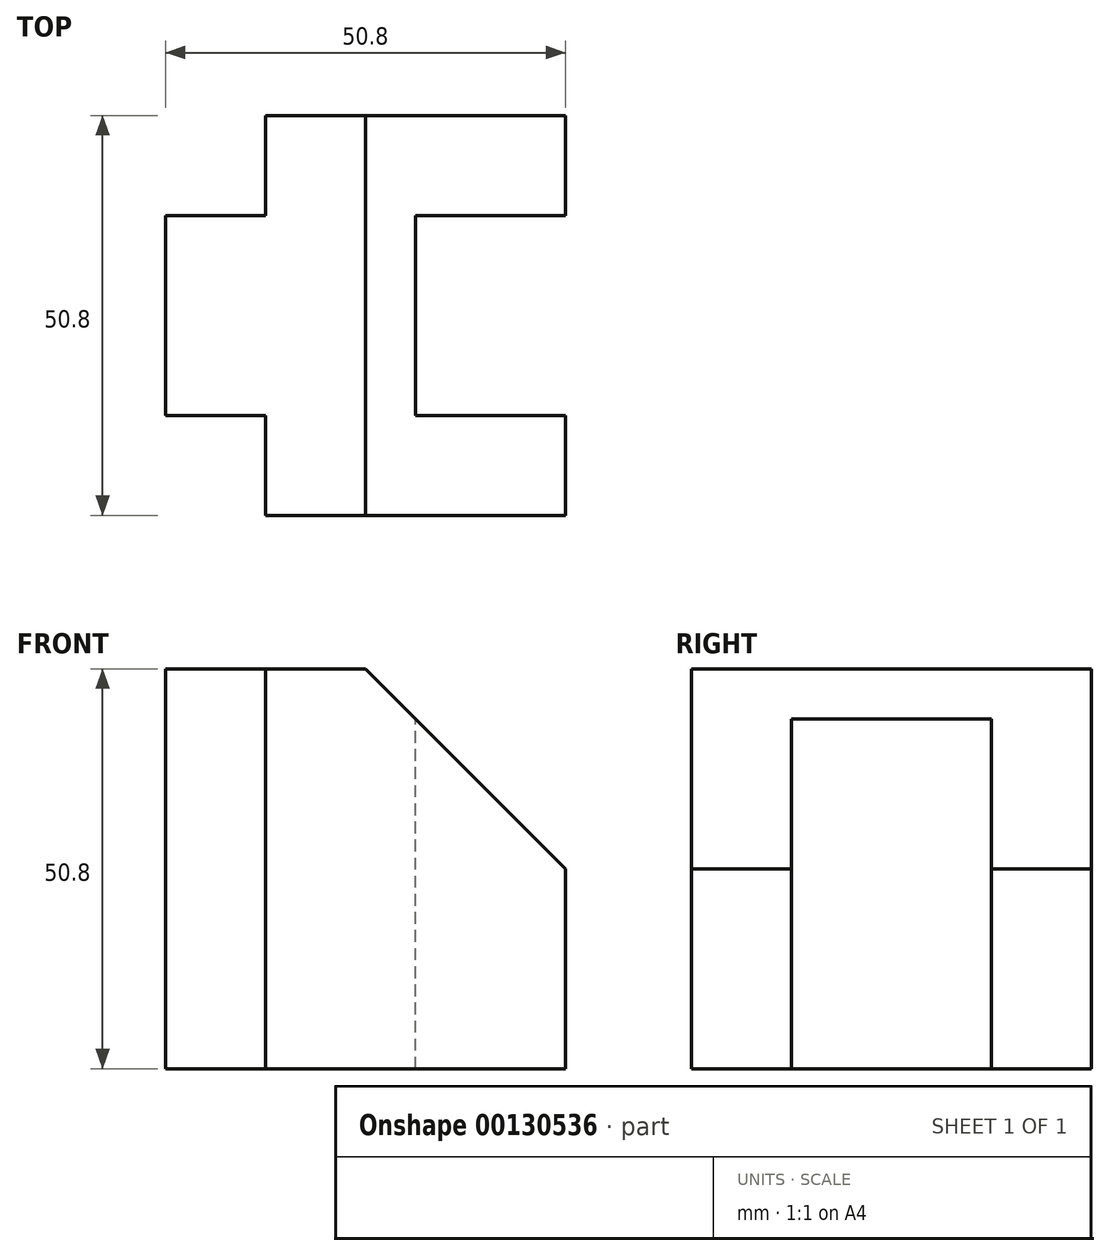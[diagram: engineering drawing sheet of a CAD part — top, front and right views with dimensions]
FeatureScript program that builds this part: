
annotation { "Feature Type Name" : "Feature", "Feature Type Description" : "" }
export const myFeature = defineFeature(function(context is Context, id is Id, definition is map)
    precondition{}
    {
        {
            var Q0;
            Q0=qCreatedBy(makeId("Top.planeOp"),FACE);
            var sketch = newSketch(context, id + "F0", { "sketchPlane" : qUnion([Q0])});
            skLineSegment(sketch, "E0", {"start": v(0, 0) * mm, "end": v(0, 12.7) * mm});
            skLineSegment(sketch, "E1", {"start": v(0, 12.7) * mm, "end": v(0, 12.7) * mm});
            skLineSegment(sketch, "E2", {"start": v(0, 12.7) * mm, "end": v(0, 38.1) * mm});
            skLineSegment(sketch, "E3", {"start": v(0, 38.1) * mm, "end": v(0, 38.1) * mm});
            skLineSegment(sketch, "E4", {"start": v(0, 38.1) * mm, "end": v(0, 50.8) * mm});
            skLineSegment(sketch, "E5", {"start": v(0, 50.8) * mm, "end": v(-38.1, 50.8) * mm});
            skLineSegment(sketch, "E6", {"start": v(-38.1, 50.8) * mm, "end": v(-38.1, 38.1) * mm});
            skLineSegment(sketch, "E7", {"start": v(-38.1, 38.1) * mm, "end": v(-50.8, 38.1) * mm});
            skLineSegment(sketch, "E8", {"start": v(-50.8, 38.1) * mm, "end": v(-50.8, 12.7) * mm});
            skLineSegment(sketch, "E9", {"start": v(-50.8, 12.7) * mm, "end": v(-38.1, 12.7) * mm});
            skLineSegment(sketch, "E10", {"start": v(-38.1, 12.7) * mm, "end": v(-38.1, 0) * mm});
            skLineSegment(sketch, "E11", {"start": v(-38.1, 0) * mm, "end": v(0, 0) * mm});
            skSolve(sketch);
        }
        {
            var Q0;
            Q0 = qSketchRegion(id + "F0", true);
            extrude(context, id + "F1", {"entities" : qUnion([Q0]), "depth" : 50.8 * mm});
        }
        {
            var Q0;
            Q0=makeQuery(id+"F1.opExtrude","SWEPT_FACE",FACE,{"disambiguationData":[OSD([sQuery(id+"F0.wireOp",EDGE,"E11")])]});
            var sketch = newSketch(context, id + "F2", { "sketchPlane" : qUnion([Q0])});
            skLineSegment(sketch, "E12", {"start": v(-25.4, 50.8) * mm, "end": v(0, 25.4) * mm});
            skLineSegment(sketch, "E13", {"start": v(0, 25.4) * mm, "end": v(0, 50.8) * mm});
            skLineSegment(sketch, "E14", {"start": v(0, 50.8) * mm, "end": v(-25.4, 50.8) * mm});
            skSolve(sketch);
        }
        {
            var Q0;
            Q0 = qSketchRegion(id + "F2", true);
            extrude(context, id + "F3", {"entities" : qUnion([Q0]), "operationType" : NewBodyOperationType.REMOVE, "endBound" : BoundingType.THROUGH_ALL, "oppositeDirection" : true, "depth" : 25.4 * mm});
        }
        {
            var Q0;
            Q0=makeQuery(id+"F1.opExtrude","CAP_FACE",FACE,{"disambiguationData":[OSD([sQuery(id+"F0.wireOp",EDGE,"E0"),sQuery(id+"F0.wireOp",EDGE,"E2"),sQuery(id+"F0.wireOp",EDGE,"E4"),sQuery(id+"F0.wireOp",EDGE,"E5"),sQuery(id+"F0.wireOp",EDGE,"E6"),sQuery(id+"F0.wireOp",EDGE,"E7"),sQuery(id+"F0.wireOp",EDGE,"E8"),sQuery(id+"F0.wireOp",EDGE,"E9"),sQuery(id+"F0.wireOp",EDGE,"E10"),sQuery(id+"F0.wireOp",EDGE,"E11")])],"isStart":false});
            var sketch = newSketch(context, id + "F4", { "sketchPlane" : qUnion([Q0])});
            skLineSegment(sketch, "E15", {"start": v(0, 38.1) * mm, "end": v(-19.05, 38.1) * mm});
            skLineSegment(sketch, "E16", {"start": v(-19.05, 38.1) * mm, "end": v(-19.05, 12.7) * mm});
            skLineSegment(sketch, "E17", {"start": v(-19.05, 12.7) * mm, "end": v(0, 12.7) * mm});
            skLineSegment(sketch, "E18", {"start": v(0, 12.7) * mm, "end": v(0, 38.1) * mm});
            skSolve(sketch);
        }
        {
            var Q0;
            Q0 = qSketchRegion(id + "F4", true);
            extrude(context, id + "F5", {"entities" : qUnion([Q0]), "operationType" : NewBodyOperationType.REMOVE, "endBound" : BoundingType.THROUGH_ALL, "oppositeDirection" : true, "depth" : 25.4 * mm});
        }
    });
